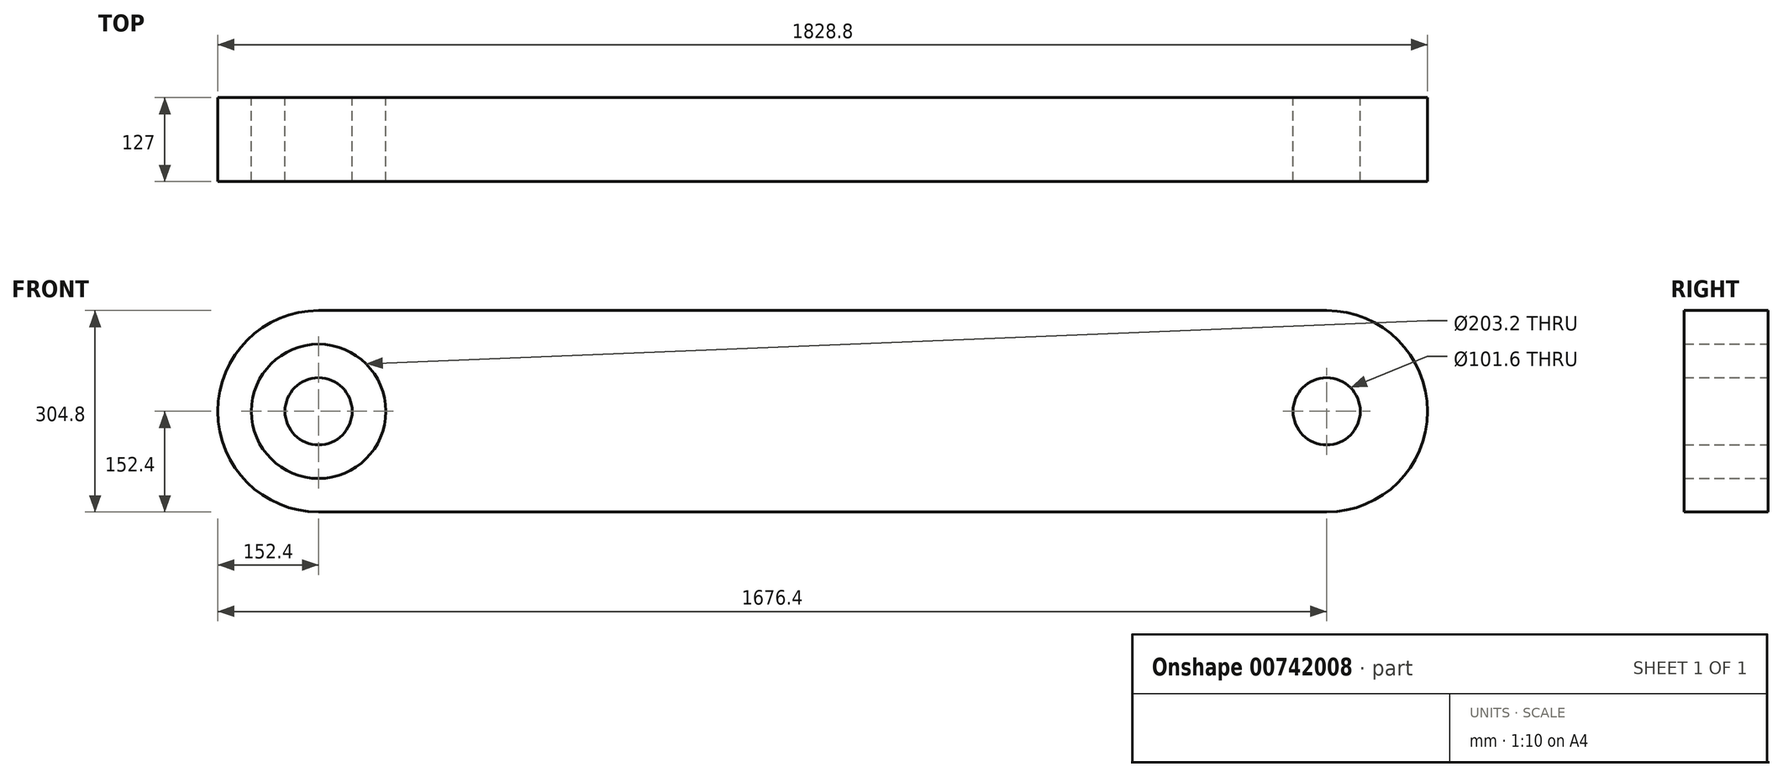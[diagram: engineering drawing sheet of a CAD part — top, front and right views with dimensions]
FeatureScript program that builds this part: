
annotation { "Feature Type Name" : "Feature", "Feature Type Description" : "" }
export const myFeature = defineFeature(function(context is Context, id is Id, definition is map)
    precondition{}
    {
        {
            var Q0;
            Q0=qCreatedBy(makeId("Front.planeOp"),FACE);
            var sketch = newSketch(context, id + "F0", { "sketchPlane" : qUnion([Q0])});
            skCircle(sketch, "E0", {"center": v(-762, 0) * mm, "radius": 50.8 * mm});
            skCircle(sketch, "E1", {"center": v(-762, 0) * mm, "radius": 101.6 * mm});
            skCircle(sketch, "E2", {"center": v(-762, 0) * mm, "radius": 152.4 * mm});
            skLineSegment(sketch, "E3", {"start": v(-762, 152.4) * mm, "end": v(0, 152.4) * mm});
            skLineSegment(sketch, "E4.MirrorCS", {"start": v(-762, -152.4) * mm, "end": v(0, -152.4) * mm});
            skCircle(sketch, "E5.MirrorC", {"center": v(762, 0) * mm, "radius": 152.4 * mm});
            skCircle(sketch, "E6.MirrorC", {"center": v(762, 0) * mm, "radius": 101.6 * mm});
            skLineSegment(sketch, "E7.MirrorCS", {"start": v(762, 152.4) * mm, "end": v(0, 152.4) * mm});
            skCircle(sketch, "E8.MirrorC", {"center": v(762, 0) * mm, "radius": 50.8 * mm});
            skLineSegment(sketch, "E9.MirrorCS", {"start": v(762, -152.4) * mm, "end": v(0, -152.4) * mm});
            skSolve(sketch);
        }
        {
            var Q0;
            Q0 = qSketchRegion(id + "F0", true);
            var Q1;
            Q1=makeQuery(id+"F0.imprint","IMPRINT",FACE,{"disambiguationData":[TD([[makeQuery(id+"F0.imprint","IMPRINT",EDGE,{"derivedFrom":sQuery(id+"F0.wireOp",EDGE,"E0")}),1.0]])]});
            var Q2;
            Q2=makeQuery(id+"F0.imprint","IMPRINT",FACE,{"disambiguationData":[TD([[makeQuery(id+"F0.imprint","IMPRINT",EDGE,{"derivedFrom":sQuery(id+"F0.wireOp",EDGE,"E8.MirrorC")}),-1.0]])]});
            extrude(context, id + "F1", {"entities" : qUnion([Q0, Q1, Q2]), "endBound" : BoundingType.SYMMETRIC, "depth" : 127 * mm, "offsetDistance" : 25.4 * mm});
        }
    });
